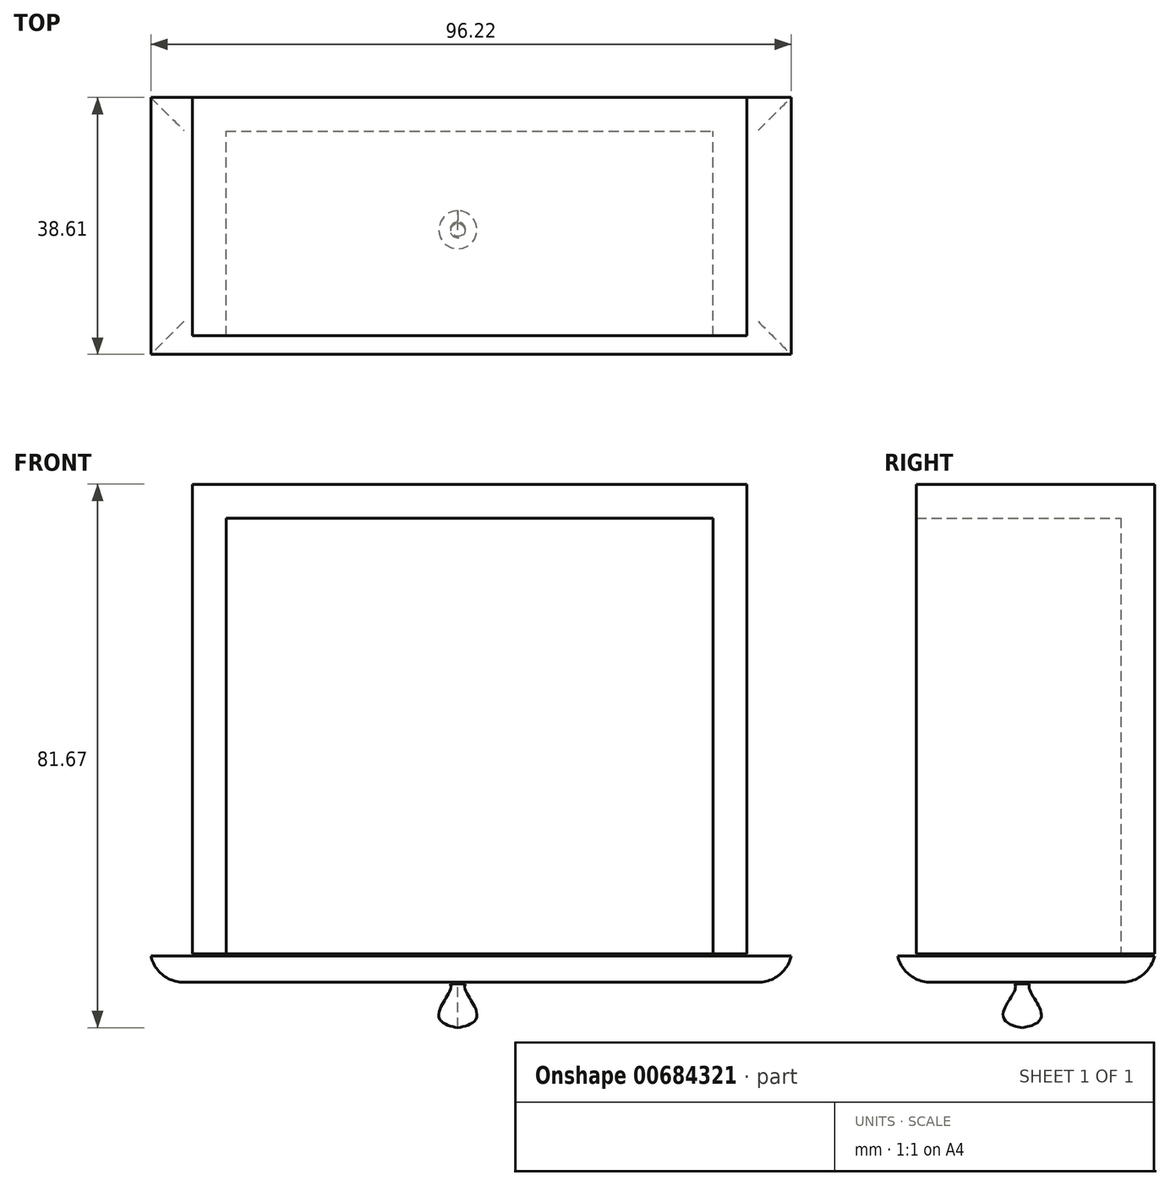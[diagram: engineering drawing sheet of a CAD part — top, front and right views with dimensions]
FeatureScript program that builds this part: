
annotation { "Feature Type Name" : "Feature", "Feature Type Description" : "" }
export const myFeature = defineFeature(function(context is Context, id is Id, definition is map)
    precondition{}
    {
        {
            var Q0;
            Q0=qCreatedBy(makeId("Front.planeOp"),FACE);
            var sketch = newSketch(context, id + "F0", { "sketchPlane" : qUnion([Q0])});
            skLineSegment(sketch, "E0.bottom", {"start": v(-39.91, 35.86) * mm, "end": v(43.42, 35.86) * mm});
            skLineSegment(sketch, "E0.top", {"start": v(-39.91, -34.75) * mm, "end": v(43.42, -34.75) * mm});
            skLineSegment(sketch, "E0.left", {"start": v(-39.91, 35.86) * mm, "end": v(-39.91, -34.75) * mm});
            skLineSegment(sketch, "E0.right", {"start": v(43.42, 35.86) * mm, "end": v(43.42, -34.75) * mm});
            skSolve(sketch);
        }
        {
            var Q0;
            Q0 = qSketchRegion(id + "F0", true);
            extrude(context, id + "F1", {"entities" : qUnion([Q0]), "depth" : 35.81 * mm, "offsetDistance" : 25.4 * mm});
        }
        {
            var Q0;
            Q0=makeQuery(id+"F1.opExtrude","CAP_FACE",FACE,{"disambiguationData":[OSD([sQuery(id+"F0.wireOp",EDGE,"E0.bottom"),sQuery(id+"F0.wireOp",EDGE,"E0.top"),sQuery(id+"F0.wireOp",EDGE,"E0.left"),sQuery(id+"F0.wireOp",EDGE,"E0.right")])],"isStart":false});
            var Q1;
            Q1=makeQuery(id+"F1.opExtrude","SWEPT_FACE",FACE,{"disambiguationData":[OSD([sQuery(id+"F0.wireOp",EDGE,"E0.top")])]});
            shell(context, id + "F2", {"entities" : qUnion([Q0, Q1]), "thickness" : 5.08 * mm});
        }
        {
            var Q0;
            Q0=qCreatedBy(makeId("Front.planeOp"),FACE);
            var sketch = newSketch(context, id + "F3", { "sketchPlane" : qUnion([Q0])});
            skLineSegment(sketch, "E1", {"start": v(-46.13, -35.01) * mm, "end": v(50.1, -35.01) * mm});
            skLineSegment(sketch, "E2", {"start": v(-46.13, -39) * mm, "end": v(50.1, -39) * mm});
            skLineSegment(sketch, "E3", {"start": v(-46.13, -35.01) * mm, "end": v(-46.13, -39) * mm});
            skLineSegment(sketch, "E4", {"start": v(50.1, -35.01) * mm, "end": v(50.1, -39) * mm});
            skSolve(sketch);
        }
        {
            var Q0;
            Q0 = qSketchRegion(id + "F3", true);
            extrude(context, id + "F4", {"entities" : qUnion([Q0]), "depth" : 38.6 * mm, "offsetDistance" : 25.4 * mm});
        }
        {
            var Q0;
            Q0=makeQuery(id+"F4.opExtrude","CAP_EDGE",EDGE,{"disambiguationData":[OSD([sQuery(id+"F3.wireOp",EDGE,"E2")])],"isStart":false});
            var Q1;
            Q1=makeQuery(id+"F4.opExtrude","SWEPT_EDGE",EDGE,{"disambiguationData":[OSD([sQuery(id+"F3.wireOp",EDGE,"E2"),sQuery(id+"F3.wireOp",EDGE,"E4")])]});
            var Q2;
            Q2=makeQuery(id+"F4.opExtrude","CAP_EDGE",EDGE,{"disambiguationData":[OSD([sQuery(id+"F3.wireOp",EDGE,"E2")])],"isStart":true});
            var Q3;
            Q3=makeQuery(id+"F4.opExtrude","SWEPT_EDGE",EDGE,{"disambiguationData":[OSD([sQuery(id+"F3.wireOp",EDGE,"E2"),sQuery(id+"F3.wireOp",EDGE,"E3")])]});
            fillet(context, id + "F5", {"entities" : qUnion([Q0, Q1, Q2, Q3]), "radius" : 5.08 * mm, "tangentPropagation" : true, "allowEdgeOverflow" : false});
        }
        {
            var Q0;
            Q0=qCreatedBy(makeId("Right.planeOp"),FACE);
            var sketch = newSketch(context, id + "F6", { "sketchPlane" : qUnion([Q0])});
            skLineSegment(sketch, "E5", {"start": v(-19.89, -39.25) * mm, "end": v(-19.89, -45.81) * mm});
            skPoint(sketch, "E6", {"position": v(-18.73, -39.25) * mm});
            skFitSpline(sketch, "E7", {"points": [v(-19.89, -45.81) * mm, v(-18.73, -39.25) * mm], "startDerivative": vector(19.1, 2.89) * mm, "endDerivative": vector(3.48, 4) * mm});
            skLineSegment(sketch, "E8", {"start": v(-18.73, -39.25) * mm, "end": v(-19.89, -39.25) * mm});
            skSolve(sketch);
        }
        {
            var Q0;
            Q0=makeQuery(id+"F6.imprint","IMPRINT",FACE,{"disambiguationData":[TD([[makeQuery(id+"F6.imprint","IMPRINT",EDGE,{"derivedFrom":sQuery(id+"F6.wireOp",EDGE,"E5")}),1.0]])]});
            var Q1;
            Q1=sQuery(id+"F6.wireOp",EDGE,"E5");
            revolve(context, id + "F7", {"entities" : qUnion([Q0]), "axis" : qUnion([Q1]), "revolveType" : RevolveType.FULL});
        }
    });
